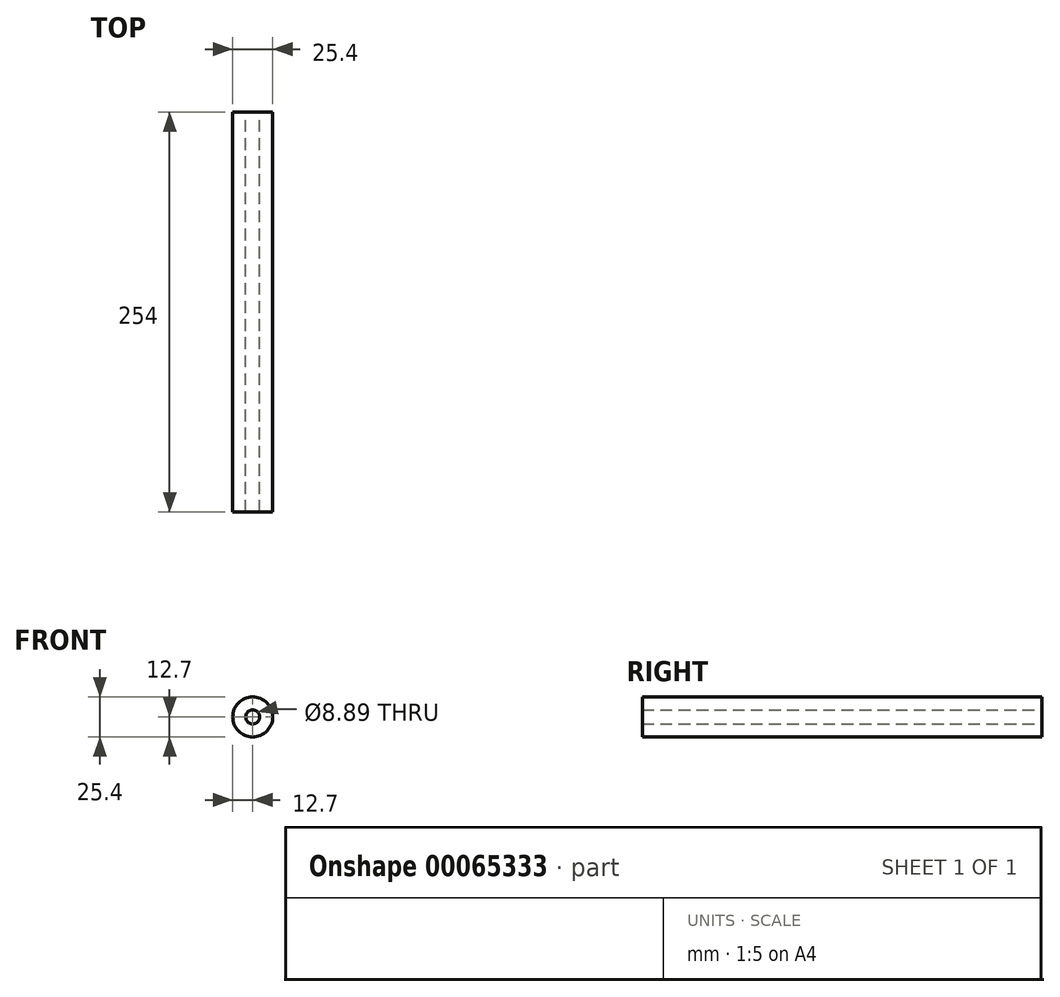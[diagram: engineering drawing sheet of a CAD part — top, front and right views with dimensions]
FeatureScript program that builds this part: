
annotation { "Feature Type Name" : "Feature", "Feature Type Description" : "" }
export const myFeature = defineFeature(function(context is Context, id is Id, definition is map)
    precondition{}
    {
        {
            var Q0;
            Q0=qCreatedBy(makeId("Front.planeOp"),FACE);
            var sketch = newSketch(context, id + "F0", { "sketchPlane" : qUnion([Q0])});
            skCircle(sketch, "E0", {"center": v(0, 0) * mm, "radius": 12.7 * mm});
            skSolve(sketch);
        }
        {
            var Q0;
            Q0=qCreatedBy(makeId("Front.planeOp"),FACE);
            var sketch = newSketch(context, id + "F1", { "sketchPlane" : qUnion([Q0])});
            skCircle(sketch, "E1", {"center": v(0, 0) * mm, "radius": 4.45 * mm});
            skSolve(sketch);
        }
        {
            var Q0;
            Q0=makeQuery(id+"F0.imprint","IMPRINT",FACE,{"disambiguationData":[TD([[makeQuery(id+"F0.imprint","IMPRINT",EDGE,{"derivedFrom":sQuery(id+"F0.wireOp",EDGE,"E0")}),1.0]])]});
            extrude(context, id + "F2", {"entities" : qUnion([Q0]), "depth" : 254 * mm});
        }
        {
            var Q0;
            Q0 = qSketchRegion(id + "F1", true);
            extrude(context, id + "F3", {"entities" : qUnion([Q0]), "operationType" : NewBodyOperationType.REMOVE, "depth" : 254 * mm});
        }
    });
